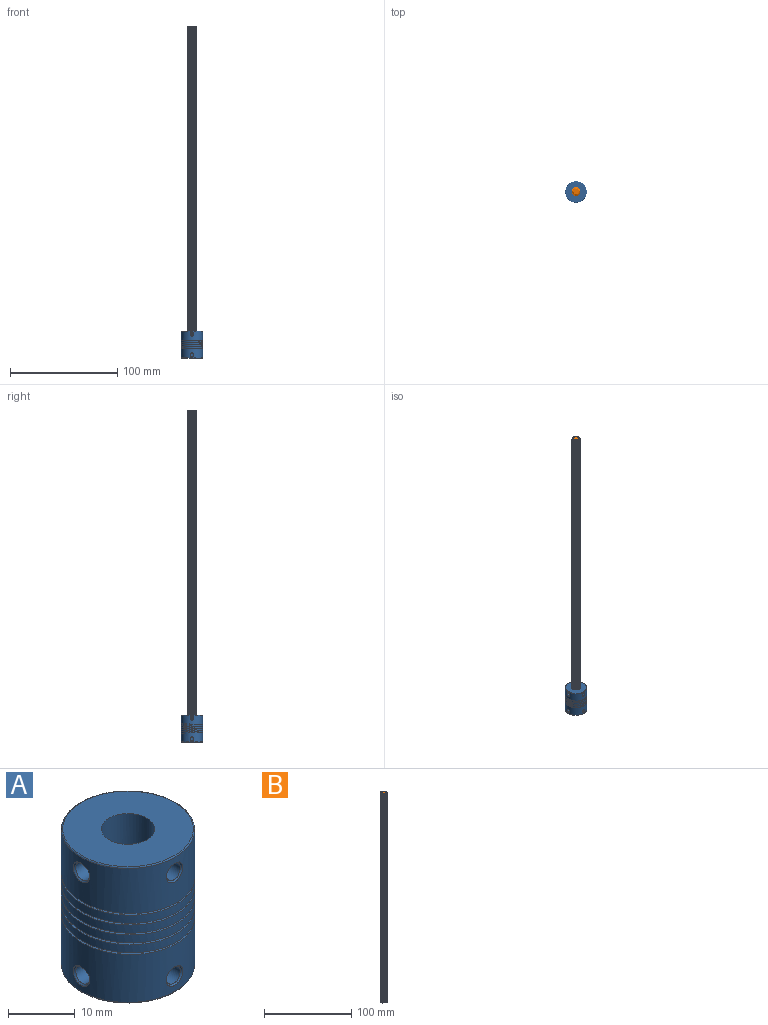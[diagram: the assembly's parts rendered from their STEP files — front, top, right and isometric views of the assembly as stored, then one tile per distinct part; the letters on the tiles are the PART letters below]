
ASSEMBLY  parts=2 mates=1
PART A: 29 faces, bbox 22x22x25 mm
  f0: cylinder r=2.5mm len=6.9mm, axis (0,0,-1), area 93.5mm2, adj f14,f15,f19,f25
  f1: bspline ~22.02x22.02mm, area 1345.9mm2, adj f3,f4,f5,f6,f7,f10,f11,f20
  f2: bspline ~22.02x22.02mm, area 1346.4mm2, adj f3,f4,f5,f6,f7,f10,f11,f20
  f3: cylinder r=10mm len=20mm, axis (0,0,-1), area 586.1mm2, adj f1,f2,f5,f11,f13,f17,f27
  f4: cylinder r=10mm len=20mm, axis (0,0,-1), area 541.6mm2, adj f1,f2,f7,f10,f12,f18,f28
  f5: cylinder r=10mm len=20mm, axis (0,0,-1), area 94.5mm2, adj f1,f2,f3,f6
  f6: cylinder r=10mm len=20mm, axis (0,0,-1), area 94.5mm2, adj f1,f2,f5,f7
  f7: cylinder r=10mm len=20mm, axis (0,0,-1), area 94.5mm2, adj f1,f2,f4,f6
  f8: plane 19.6x19.6mm, normal (0,0,1), area 251.5mm2, adj f13,f24
  f9: plane 19.6x19.6mm, normal (0,0,-1), area 280.5mm2, adj f12,f14
  f10: plane 4.24x4.24mm, normal (0.71,0.71,0), area 1.8mm2, adj f1,f2,f4,f20
  f11: plane 5.93x0.94mm, normal (-0.99,-0.16,0), area 1.8mm2, adj f1,f2,f3,f24
  f12: torus R=9.8mm, axis (0,0,1), area 19.6mm2, adj f4,f9
  f13: torus R=9.8mm, axis (0,0,1), area 19.6mm2, adj f3,f8
  f14: cone r=2.5mm half-angle=45deg, axis (0,0,-1), area 2.3mm2, adj f0,f9
  f15: cylinder r=1.5mm len=7.24mm, axis (1,0,0), area 68.2mm2, adj f0,f18
  f16: cylinder r=1.5mm len=5.74mm, axis (1,0,0), area 54.1mm2, adj f17,f24
  f17: bspline ~3.52x3.42mm, area 3.6mm2, adj f3,f16
  f18: bspline ~3.52x3.42mm, area 3.6mm2, adj f4,f15
  f19: plane 8x8mm, normal (0,0,1), area 30.6mm2, adj f0,f20
  f20: cylinder r=4mm len=8mm, axis (0,0,1), area 53.4mm2, adj f1,f2,f10,f19,f21
  f21: cylinder r=4mm len=8mm, axis (0,0,1), area 37.8mm2, adj f1,f2,f20,f22
  f22: cylinder r=4mm len=8mm, axis (0,0,1), area 37.8mm2, adj f1,f2,f21,f23
  f23: cylinder r=4mm len=8mm, axis (0,0,1), area 37.8mm2, adj f1,f2,f22,f24
  f24: cylinder r=4mm len=10.95mm, axis (0,0,1), area 232.7mm2, adj f1,f2,f8,f11,f16,f23,f26
  f25: cylinder r=1.5mm len=7.24mm, axis (0,1,0), area 68.2mm2, adj f0,f28
  f26: cylinder r=1.5mm len=5.74mm, axis (0,1,0), area 54.1mm2, adj f24,f27
  f27: bspline ~3.52x3.42mm, area 3.6mm2, adj f3,f26
  f28: bspline ~3.52x3.42mm, area 3.6mm2, adj f4,f25
PART B: 20 faces, bbox 8x8.2x294 mm
  f0: cone r=2.5mm half-angle=60deg, axis (0,0,-1), area 22.2mm2, adj f1,f2,f3,f4,f5,f6,f7,f8
  f1: cone r=2.5mm half-angle=60deg, axis (0,0,-1), area 0.3mm2, adj f0,f4,f12
  f2: cylinder r=4mm len=292.13mm, axis (0,0,1), area 673.7mm2, adj f0,f6,f11,f19
  f3: cylinder r=4mm len=292.13mm, axis (0,0,1), area 673.7mm2, adj f0,f9,f14,f19
  f4: cylinder r=4mm len=292.13mm, axis (0,0,1), area 673.7mm2, adj f0,f1,f12,f17,f19
  f5: cylinder r=4mm len=292.13mm, axis (0,0,1), area 673.7mm2, adj f0,f8,f15,f19
  f6: bspline ~293.98x8.21mm, area 882.4mm2, adj f0,f2,f7,f19
  f7: cylinder r=3mm len=292.71mm, axis (0,0,1), area 357.2mm2, adj f0,f6,f8,f19
  f8: bspline ~293.41x8.21mm, area 882.4mm2, adj f0,f5,f7,f19
  f9: bspline ~292.98x7.97mm, area 882.3mm2, adj f0,f3,f10,f19
  f10: cylinder r=3mm len=292.71mm, axis (0,0,1), area 357.2mm2, adj f0,f9,f11,f19
  f11: bspline ~293.25x8mm, area 882.4mm2, adj f0,f2,f10,f19
  f12: bspline ~293.98x8.21mm, area 882.4mm2, adj f0,f1,f4,f13,f19
  f13: cylinder r=3mm len=292.71mm, axis (0,0,1), area 357.2mm2, adj f0,f12,f14,f19
  f14: bspline ~293.41x8.21mm, area 882.4mm2, adj f0,f3,f13,f19
  f15: bspline ~292.98x7.97mm, area 882.3mm2, adj f0,f5,f16,f19
  f16: cylinder r=3mm len=292.71mm, axis (0,0,1), area 357.2mm2, adj f0,f15,f17,f19
  f17: bspline ~293.25x8mm, area 882.4mm2, adj f0,f4,f16,f19
  f18: plane 5x5mm, normal (0,0,1), area 19.6mm2, adj f0
  f19: plane 8.03x8.03mm, normal (0,0,-1), area 39.2mm2, adj f2,f3,f4,f5,f6,f7,f8,f9
PLACE A at identity fixed
PLACE B t=(0,0,310)mm
MATE fastened B.f13 <-> A.f0  axis (0,0,-1) through (0,0,17)mm
